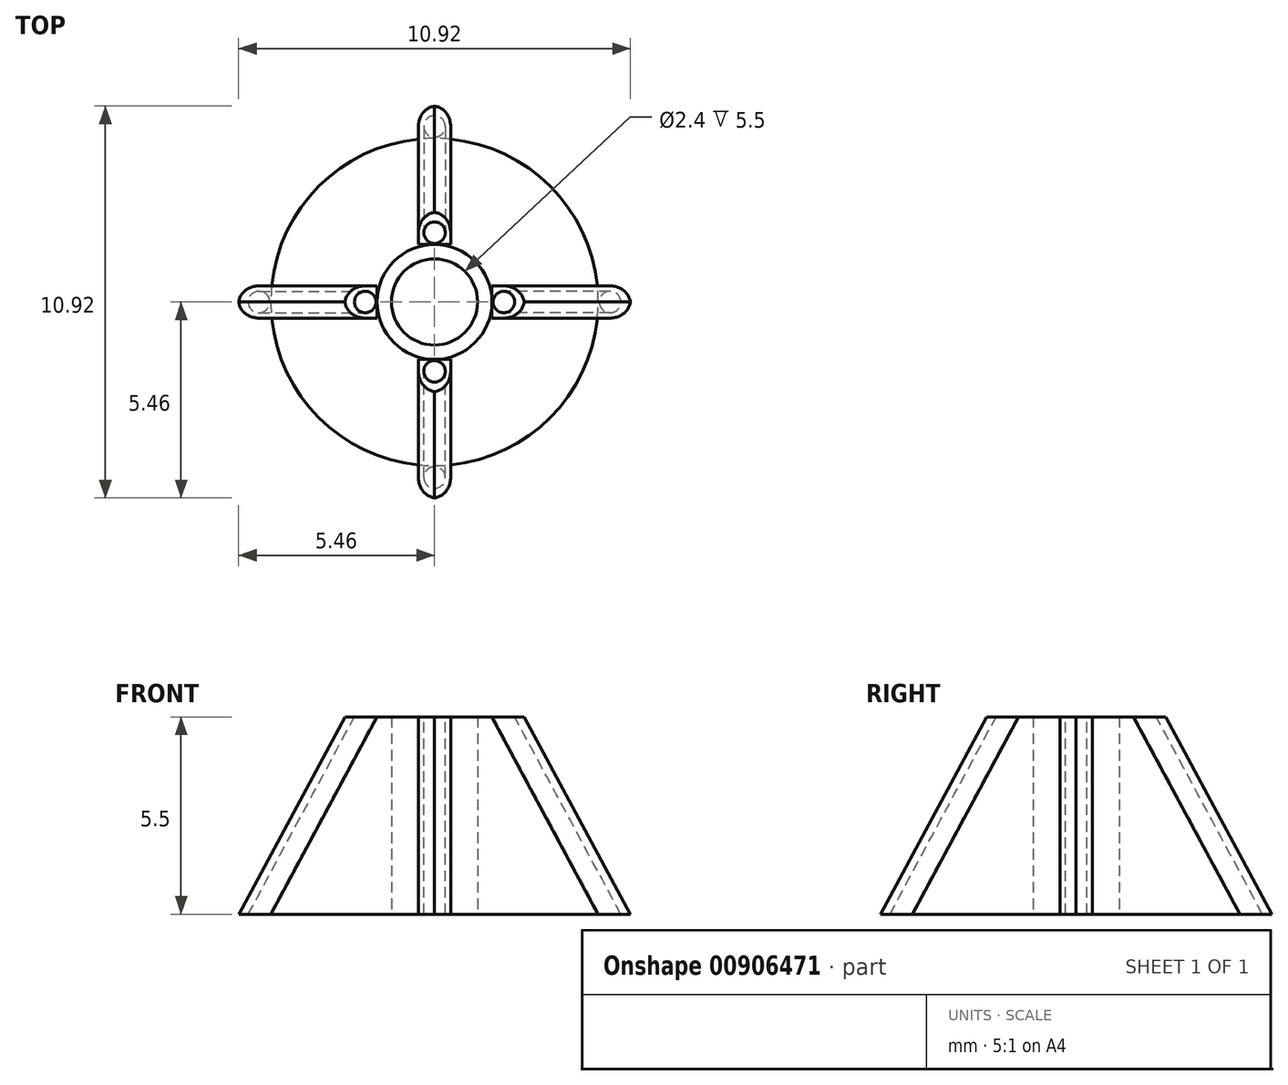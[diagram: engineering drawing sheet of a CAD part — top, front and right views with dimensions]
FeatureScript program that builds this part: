
annotation { "Feature Type Name" : "Feature", "Feature Type Description" : "" }
export const myFeature = defineFeature(function(context is Context, id is Id, definition is map)
    precondition{}
    {
        {
            var Q0;
            Q0=qCreatedBy(makeId("Front.planeOp"),FACE);
            var sketch = newSketch(context, id + "F0", { "sketchPlane" : qUnion([Q0])});
            skLineSegment(sketch, "E0", {"start": v(-1.2, 5.5) * mm, "end": v(-1.6, 5.5) * mm});
            skLineSegment(sketch, "E1", {"start": v(-1.6, 5.5) * mm, "end": v(-4.56, 0) * mm});
            skLineSegment(sketch, "E2", {"start": v(-4.56, 0) * mm, "end": v(-1.2, 0) * mm});
            skLineSegment(sketch, "E3", {"start": v(-1.2, 0) * mm, "end": v(-1.2, 5.5) * mm});
            skLineSegment(sketch, "E4", {"start": v(-1.2, 0) * mm, "end": v(0, 0) * mm, "construction": true});
            skLineSegment(sketch, "E5", {"start": v(0, 0) * mm, "end": v(0, 5.5) * mm, "construction": true});
            skLineSegment(sketch, "E6", {"start": v(0, 5.5) * mm, "end": v(-1.2, 5.5) * mm, "construction": true});
            skSolve(sketch);
        }
        {
            var Q0;
            Q0=makeQuery(id+"F0.imprint","IMPRINT",FACE,{"disambiguationData":[TD([[makeQuery(id+"F0.imprint","IMPRINT",EDGE,{"derivedFrom":sQuery(id+"F0.wireOp",EDGE,"E0")}),1.0]])]});
            var Q1;
            Q1=sQuery(id+"F0.wireOp",EDGE,"E5");
            revolve(context, id + "F1", {"surfaceOperationType" : NewSurfaceOperationType.NEW, "entities" : qUnion([Q0]), "axis" : qUnion([Q1]), "revolveType" : RevolveType.FULL});
        }
        {
            var Q0;
            Q0=qCreatedBy(makeId("Front.planeOp"),FACE);
            var sketch = newSketch(context, id + "F2", { "sketchPlane" : qUnion([Q0])});
            skLineSegment(sketch, "E7", {"start": v(-4.56, 0) * mm, "end": v(-5.46, 0) * mm});
            skLineSegment(sketch, "E8", {"start": v(-5.46, 0) * mm, "end": v(-2.5, 5.5) * mm});
            skLineSegment(sketch, "E9", {"start": v(-2.5, 5.5) * mm, "end": v(-1.6, 5.5) * mm});
            skLineSegment(sketch, "E10", {"start": v(-4.56, 0) * mm, "end": v(-1.6, 5.5) * mm});
            skSolve(sketch);
        }
        {
            var Q0;
            Q0=makeQuery(id+"F2.imprint","IMPRINT",FACE,{"disambiguationData":[TD([[makeQuery(id+"F2.imprint","IMPRINT",EDGE,{"derivedFrom":sQuery(id+"F2.wireOp",EDGE,"E7")}),-1.0]])]});
            extrude(context, id + "F3", {"entities" : qUnion([Q0]), "endBound" : BoundingType.SYMMETRIC, "depth" : 0.9 * mm, "offsetDistance" : 25 * mm});
        }
        {
            var Q0;
            Q0=makeQuery(id+"F3.opExtrude","CAP_EDGE",EDGE,{"disambiguationData":[OSD([sQuery(id+"F2.wireOp",EDGE,"E8")])],"isStart":true});
            var Q1;
            Q1=makeQuery(id+"F3.opExtrude","CAP_EDGE",EDGE,{"disambiguationData":[OSD([sQuery(id+"F2.wireOp",EDGE,"E8")])],"isStart":false});
            fillet(context, id + "F4", {"entities" : qUnion([Q0, Q1]), "radius" : 0.5 * mm, "rho" : 0, "crossSection" : FilletCrossSection.CONIC, "allowEdgeOverflow" : false});
        }
        {
            var Q0;
            Q0=makeQuery(id+"F3.opExtrude","SWEPT_FACE",FACE,{"disambiguationData":[OSD([sQuery(id+"F2.wireOp",EDGE,"E9")])]});
            var sketch = newSketch(context, id + "F5", { "sketchPlane" : qUnion([Q0])});
            skCircle(sketch, "E11", {"center": v(-1.93, 0) * mm, "radius": 0.3 * mm});
            skSolve(sketch);
        }
        {
            var Q0;
            Q0=makeQuery(id+"F3.opExtrude","SWEPT_FACE",FACE,{"disambiguationData":[OSD([sQuery(id+"F2.wireOp",EDGE,"E7")])]});
            var sketch = newSketch(context, id + "F6", { "sketchPlane" : qUnion([Q0])});
            skCircle(sketch, "E12", {"center": v(-4.9, 0) * mm, "radius": 0.3 * mm});
            skSolve(sketch);
        }
        {
            var Q1;
            Q1=makeQuery(id+"F5.imprint","IMPRINT",FACE,{"disambiguationData":[TD([[makeQuery(id+"F5.imprint","IMPRINT",EDGE,{"derivedFrom":sQuery(id+"F5.wireOp",EDGE,"E11")}),1.0]])]});
            var Q2;
            Q2=makeQuery(id+"F6.imprint","IMPRINT",FACE,{"disambiguationData":[TD([[makeQuery(id+"F6.imprint","IMPRINT",EDGE,{"derivedFrom":sQuery(id+"F6.wireOp",EDGE,"E12")}),1.0]])]});
            loft(context, id + "F7", {"operationType" : NewBodyOperationType.REMOVE, "sheetProfilesArray" : [{ "sheetProfileEntities" : qUnion([Q1]) }, { "sheetProfileEntities" : qUnion([Q2]) }]});
        }
        {
            var Q0;
            Q0=makeQuery(id+"F3.opExtrude","SWEPT_BODY",BODY,{"disambiguationData":[OSD([sQuery(id+"F2.wireOp",EDGE,"E7"),sQuery(id+"F2.wireOp",EDGE,"E8"),sQuery(id+"F2.wireOp",EDGE,"E9"),sQuery(id+"F2.wireOp",EDGE,"E10")])]});
            var Q1;
            Q1=makeQuery(id+"F1.opRevolve","SWEPT_EDGE",EDGE,{"disambiguationData":[OSD([sQuery(id+"F0.wireOp",EDGE,"E0"),sQuery(id+"F0.wireOp",EDGE,"E1")])]});
            circularPattern(context, id + "F8", {"entities" : qUnion([Q0]), "axis" : qUnion([Q1]), "angle" : 360 * degree, "instanceCount" : 4, "equalSpace" : true});
        }
    });
